# Revit family: Door-Exterior_Interior-Simpson-French-Full_Decorative_Arch_Glass-Single
name_source: partatom
category: Doors
revit_build: Autodesk Revit Architecture 2012 (Build: 20110916_2132(x64)
units: mm (PartAtom-declared; Revit-internal decimal feet)

## types (63) — shared parameters
Arch Bottom Height = 0' - 6 15/16"
Assembly Code = B2030230
Bottom Rail Height = 0' - 8 11/16"
Construction Type = Wood
Frame = Wood - Simpson Doors - Douglas Fir
Frame Projection Ext. = 0' - 1"
Frame Projection Int. = 0' - 1"
Frame Type = Frame : Standard
Frame Width = 0' - 3"
Function = Exterior
Glass = Glass - Simpson Doors - Clear
Glass Options = http://simpsondoor.com
Manufacturer = Simpsons Door Company
Muntin Width = 0' - 0 1/2"
Number of Horizontal Muntins = 4
Number of Vertical Muntins = 1
Ovolo Construction = Yes
Panel = Wood - Simpson Doors - Douglas Fir
Panel Stile Width = 0' - 4"
Product Documentation Link = http://www.simpsondoor.com
Product Page URL = http://www.simpsondoor.com
Thickness = 0' - 1 3/4"
Thickness Note = comes in 1 3/4" and 2 1/4" Thickness. Default is set to 1 3/4"
Top Rail Height = 0' - 3 15/16"
URL = http://www.simpsondoor.com
UltraBlock Note = This Door Comes with The Option of UltraBlock Technology. It is Turn On as a Default
UltraBlock Option = Yes
Wall Closure = By host
WaterBarrier Note = This Door Comes with The Option of WaterBarrier with UltraBlock Technology. It is Turn Off as a Default
WaterBarrier with UltraBlock Technology = No
Wood Species = http://simpsondoor.com
Wood Species Note = Available in Any Wood Species

## per-type parameters (varying)
| type | Description | Height | Model | Rough Height | Rough Width | Width |
| 1580 Exterior French 30x80 Ovolo Flat Panel | Exterior French - Ten Lite | 6' - 8" | 1580 | 6' - 10" | 2' - 10" | 2' - 6" |
| 1580 Exterior French 30x84 Ovolo Flat Panel | Exterior French - Ten Lite | 7' - 0" | 1580 | 7' - 2" | 2' - 10" | 2' - 6" |
| 1580 Exterior French 30x96 Ovolo Flat Panel | Exterior French - Ten Lite | 8' - 0" | 1580 | 8' - 2" | 2' - 10" | 2' - 6" |
| 1580 Exterior French 32x80 Ovolo Flat Panel | Exterior French - Ten Lite | 6' - 8" | 1580 | 6' - 10" | 3' - 0" | 2' - 8" |
| 1580 Exterior French 32x84 Ovolo Flat Panel | Exterior French - Ten Lite | 7' - 0" | 1580 | 7' - 2" | 3' - 0" | 2' - 8" |
| 1580 Exterior French 32x96 Ovolo Flat Panel | Exterior French - Ten Lite | 8' - 0" | 1580 | 8' - 2" | 3' - 0" | 2' - 8" |
| 1580 Exterior French 34x80 Ovolo Flat Panel | Exterior French - Ten Lite | 6' - 8" | 1580 | 6' - 10" | 3' - 2" | 2' - 10" |
| 1580 Exterior French 34x84 Ovolo Flat Panel | Exterior French - Ten Lite | 7' - 0" | 1580 | 7' - 2" | 3' - 2" | 2' - 10" |
| 1580 Exterior French 34x96 Ovolo Flat Panel | Exterior French - Ten Lite | 8' - 0" | 1580 | 8' - 2" | 3' - 2" | 2' - 10" |
| 1580 Exterior French 36x80 Ovolo Flat Panel | Exterior French - Ten Lite | 6' - 8" | 1580 | 6' - 10" | 3' - 4" | 3' - 0" |
| 1580 Exterior French 36x84 Ovolo Flat Panel | Exterior French - Ten Lite | 7' - 0" | 1580 | 7' - 2" | 3' - 4" | 3' - 0" |
| 1580 Exterior French 36x96 Ovolo Flat Panel | Exterior French - Ten Lite | 8' - 0" | 1580 | 8' - 2" | 3' - 4" | 3' - 0" |
| 1580 Exterior French 38x80 Ovolo Flat Panel | Exterior French - Ten Lite | 6' - 8" | 1580 | 6' - 10" | 3' - 6" | 3' - 2" |
| 1580 Exterior French 38x84 Ovolo Flat Panel | Exterior French - Ten Lite | 7' - 0" | 1580 | 7' - 2" | 3' - 6" | 3' - 2" |
| 1580 Exterior French 38x96 Ovolo Flat Panel | Exterior French - Ten Lite | 8' - 0" | 1580 | 8' - 2" | 3' - 6" | 3' - 2" |
| 1580 Exterior French 40x80 Ovolo Flat Panel | Exterior French - Ten Lite | 6' - 8" | 1580 | 6' - 10" | 3' - 8" | 3' - 4" |
| 1580 Exterior French 40x84 Ovolo Flat Panel | Exterior French - Ten Lite | 7' - 0" | 1580 | 7' - 2" | 3' - 8" | 3' - 4" |
| 1580 Exterior French 40x96 Ovolo Flat Panel | Exterior French - Ten Lite | 8' - 0" | 1580 | 8' - 2" | 3' - 8" | 3' - 4" |
| 1580 Exterior French 42x80 Ovolo Flat Panel | Exterior French - Ten Lite | 6' - 8" | 1580 | 6' - 10" | 3' - 10" | 3' - 6" |
| 1580 Exterior French 42x84 Ovolo Flat Panel | Exterior French - Ten Lite | 7' - 0" | 1580 | 7' - 2" | 3' - 10" | 3' - 6" |
| 1580 Exterior French 42x96 Ovolo Flat Panel | Exterior French - Ten Lite | 8' - 0" | 1580 | 8' - 2" | 3' - 10" | 3' - 6" |
| 7580 Exterior French 30x80 Ovolo Flat Panel | Exterior French TDL - Ten Lite | 6' - 8" | 7580 | 6' - 10" | 2' - 10" | 2' - 6" |
| 7580 Exterior French 30x84 Ovolo Flat Panel | Exterior French TDL - Ten Lite | 7' - 0" | 7580 | 7' - 2" | 2' - 10" | 2' - 6" |
| 7580 Exterior French 30x96 Ovolo Flat Panel | Exterior French TDL - Ten Lite | 8' - 0" | 7580 | 8' - 2" | 2' - 10" | 2' - 6" |
| 7580 Exterior French 32x80 Ovolo Flat Panel | Exterior French TDL - Ten Lite | 6' - 8" | 7580 | 6' - 10" | 3' - 0" | 2' - 8" |
| 7580 Exterior French 32x84 Ovolo Flat Panel | Exterior French TDL - Ten Lite | 7' - 0" | 7580 | 7' - 2" | 3' - 0" | 2' - 8" |
| 7580 Exterior French 32x96 Ovolo Flat Panel | Exterior French TDL - Ten Lite | 8' - 0" | 7580 | 8' - 2" | 3' - 0" | 2' - 8" |
| 7580 Exterior French 34x80 Ovolo Flat Panel | Exterior French TDL - Ten Lite | 6' - 8" | 7580 | 6' - 10" | 3' - 2" | 2' - 10" |
| 7580 Exterior French 34x84 Ovolo Flat Panel | Exterior French TDL - Ten Lite | 7' - 0" | 7580 | 7' - 2" | 3' - 2" | 2' - 10" |
| 7580 Exterior French 34x96 Ovolo Flat Panel | Exterior French TDL - Ten Lite | 8' - 0" | 7580 | 8' - 2" | 3' - 2" | 2' - 10" |
| 7580 Exterior French 36x80 Ovolo Flat Panel | Exterior French TDL - Ten Lite | 6' - 8" | 7580 | 6' - 10" | 3' - 4" | 3' - 0" |
| 7580 Exterior French 36x84 Ovolo Flat Panel | Exterior French TDL - Ten Lite | 7' - 0" | 7580 | 7' - 2" | 3' - 4" | 3' - 0" |
| 7580 Exterior French 36x96 Ovolo Flat Panel | Exterior French TDL - Ten Lite | 8' - 0" | 7580 | 8' - 2" | 3' - 4" | 3' - 0" |
| 7580 Exterior French 38x80 Ovolo Flat Panel | Exterior French TDL - Ten Lite | 6' - 8" | 7580 | 6' - 10" | 3' - 6" | 3' - 2" |
| 7580 Exterior French 38x84 Ovolo Flat Panel | Exterior French TDL - Ten Lite | 7' - 0" | 7580 | 7' - 2" | 3' - 6" | 3' - 2" |
| 7580 Exterior French 38x96 Ovolo Flat Panel | Exterior French TDL - Ten Lite | 8' - 0" | 7580 | 8' - 2" | 3' - 6" | 3' - 2" |
| 7580 Exterior French 40x80 Ovolo Flat Panel | Exterior French TDL - Ten Lite | 6' - 8" | 7580 | 6' - 10" | 3' - 8" | 3' - 4" |
| 7580 Exterior French 40x84 Ovolo Flat Panel | Exterior French TDL - Ten Lite | 7' - 0" | 7580 | 7' - 2" | 3' - 8" | 3' - 4" |
| 7580 Exterior French 40x96 Ovolo Flat Panel | Exterior French TDL - Ten Lite | 8' - 0" | 7580 | 8' - 2" | 3' - 8" | 3' - 4" |
| 7580 Exterior French 42x80 Ovolo Flat Panel | Exterior French TDL - Ten Lite | 6' - 8" | 7580 | 6' - 10" | 3' - 10" | 3' - 6" |
| 7580 Exterior French 42x84 Ovolo Flat Panel | Exterior French TDL - Ten Lite | 7' - 0" | 7580 | 7' - 2" | 3' - 10" | 3' - 6" |
| 7580 Exterior French 42x96 Ovolo Flat Panel | Exterior French TDL - Ten Lite | 8' - 0" | 7580 | 8' - 2" | 3' - 10" | 3' - 6" |
| 37580 Exterior French 30x80 Ovolo Flat Panel | Exterior French SDL - Ten Lite | 6' - 8" | 37580 | 6' - 10" | 2' - 10" | 2' - 6" |
| 37580 Exterior French 30x84 Ovolo Flat Panel | Exterior French SDL - Ten Lite | 7' - 0" | 37580 | 7' - 2" | 2' - 10" | 2' - 6" |
| 37580 Exterior French 30x96 Ovolo Flat Panel | Exterior French SDL - Ten Lite | 8' - 0" | 37580 | 8' - 2" | 2' - 10" | 2' - 6" |
| 37580 Exterior French 32x80 Ovolo Flat Panel | Exterior French SDL - Ten Lite | 6' - 8" | 37580 | 6' - 10" | 3' - 0" | 2' - 8" |
| 37580 Exterior French 32x84 Ovolo Flat Panel | Exterior French SDL - Ten Lite | 7' - 0" | 37580 | 7' - 2" | 3' - 0" | 2' - 8" |
| 37580 Exterior French 32x96 Ovolo Flat Panel | Exterior French SDL - Ten Lite | 8' - 0" | 37580 | 8' - 2" | 3' - 0" | 2' - 8" |
| 37580 Exterior French 34x80 Ovolo Flat Panel | Exterior French SDL - Ten Lite | 6' - 8" | 37580 | 6' - 10" | 3' - 2" | 2' - 10" |
| 37580 Exterior French 34x84 Ovolo Flat Panel | Exterior French SDL - Ten Lite | 7' - 0" | 37580 | 7' - 2" | 3' - 2" | 2' - 10" |
| 37580 Exterior French 34x96 Ovolo Flat Panel | Exterior French SDL - Ten Lite | 8' - 0" | 37580 | 8' - 2" | 3' - 2" | 2' - 10" |
| 37580 Exterior French 36x80 Ovolo Flat Panel | Exterior French SDL - Ten Lite | 6' - 8" | 37580 | 6' - 10" | 3' - 4" | 3' - 0" |
| 37580 Exterior French 36x84 Ovolo Flat Panel | Exterior French SDL - Ten Lite | 7' - 0" | 37580 | 7' - 2" | 3' - 4" | 3' - 0" |
| 37580 Exterior French 36x96 Ovolo Flat Panel | Exterior French SDL - Ten Lite | 8' - 0" | 37580 | 8' - 2" | 3' - 4" | 3' - 0" |
| 37580 Exterior French 38x80 Ovolo Flat Panel | Exterior French SDL - Ten Lite | 6' - 8" | 37580 | 6' - 10" | 3' - 6" | 3' - 2" |
| 37580 Exterior French 38x84 Ovolo Flat Panel | Exterior French SDL - Ten Lite | 7' - 0" | 37580 | 7' - 2" | 3' - 6" | 3' - 2" |
| 37580 Exterior French 38x96 Ovolo Flat Panel | Exterior French SDL - Ten Lite | 8' - 0" | 37580 | 8' - 2" | 3' - 6" | 3' - 2" |
| 37580 Exterior French 40x80 Ovolo Flat Panel | Exterior French SDL - Ten Lite | 6' - 8" | 37580 | 6' - 10" | 3' - 8" | 3' - 4" |
| 37580 Exterior French 40x84 Ovolo Flat Panel | Exterior French SDL - Ten Lite | 7' - 0" | 37580 | 7' - 2" | 3' - 8" | 3' - 4" |
| 37580 Exterior French 40x96 Ovolo Flat Panel | Exterior French SDL - Ten Lite | 8' - 0" | 37580 | 8' - 2" | 3' - 8" | 3' - 4" |
| 37580 Exterior French 42x80 Ovolo Flat Panel | Exterior French SDL - Ten Lite | 6' - 8" | 37580 | 6' - 10" | 3' - 10" | 3' - 6" |
| 37580 Exterior French 42x84 Ovolo Flat Panel | Exterior French SDL - Ten Lite | 7' - 0" | 37580 | 7' - 2" | 3' - 10" | 3' - 6" |
| 37580 Exterior French 42x96 Ovolo Flat Panel | Exterior French SDL - Ten Lite | 8' - 0" | 37580 | 8' - 2" | 3' - 10" | 3' - 6" |

## geometry (parser evidence)
native form markers: Blend x34, Sweep x14
no freeform markers — native parametric forms only
